MODEL slx_41d5be41e8e3
CONFIG AbsTol = auto
CONFIG EnableMultiTasking = off
CONFIG FixedStep = 1e-3
CONFIG MaxStep = auto
CONFIG MinStep = auto
CONFIG RelTol = 1e-3
CONFIG SampleTimeConstraint = Unconstrained
CONFIG Solver = ode14x
CONFIG SolverName = ode14x
CONFIG StartTime = 0.0
CONFIG StopTime = 15
BLOCK [From] Actual ouput
  GotoTag = Y
BLOCK [Scope] Actual position (mm)
  Floating = off
  NumInputPorts = 1
  Ports = [1]
  ScopeSpecificationString = Simulink.scopes.TimeScopeBlockCfg('CurrentConfiguration', extmgr.ConfigurationSet(extmgr.Configuration('Core','General UI',true),extmgr.Configuration('Core','Source UI',true),extmgr.Configuration('Sources','WiredSimulink',true,'DataLoggingVariableName','ScopeData1','DataLoggingSaveFormat','Array'),extmgr.Configuration('Visuals','Time Domain',true,'SerializedDisplays',{struct('MinYLimReal','-0.1145...<+1423ch>
BLOCK [Sum] Add
  IconShape = rectangular
  Inputs = +++
  Ports = [3, 1]
BLOCK [Derivative] Derivative
BLOCK [From] Disturbance Input
  GotoTag = D
BLOCK [From] Error
  GotoTag = E
BLOCK [Gain] Force to Voltage
  Gain = 1/ 2871.14
BLOCK [FromWorkspace] From Workspace2
  OutDataTypeStr = double
  OutputAfterFinalValue = Setting to zero
  VariableName = Cut1500down
BLOCK [Goto] Goto
  GotoTag = D
BLOCK [Goto] Goto1
  GotoTag = R
BLOCK [Goto] Goto2
  GotoTag = E
BLOCK [Goto] Goto3
  GotoTag = Y
BLOCK [Integrator] Integrator
  Ports = [1, 1]
BLOCK [Gain] Kd
  Gain = new_kd
BLOCK [Gain] Ki
  Gain = new_ki
BLOCK [Gain] Kp
  Gain = new_kp
BLOCK [ManualSwitch] Manual Switch2
  CurrentSetting = 0
  NameLocation = left
BLOCK [TransferFcn] Plant (Googol Tech)
  Denominator = [1 163 193.3]
  Numerator = [78020]
BLOCK [Sin] Ref. Position, Xref (mm)
  Amplitude = 5
  Frequency = 0.5*(2*pi)
  Offset = 1/2000
  Ports = [0, 1]
  SampleTime = 0
BLOCK [From] Reference Input
  GotoTag = R
BLOCK [Saturate] Saturation
  LowerLimit = -92
  UpperLimit = 92
BLOCK [Scope] Scope
  Floating = off
  NumInputPorts = 4
  Ports = [4]
  ScopeSpecificationString = Simulink.scopes.TimeScopeBlockCfg('CurrentConfiguration', extmgr.ConfigurationSet(extmgr.Configuration('Core','General UI',true),extmgr.Configuration('Core','Source UI',true),extmgr.Configuration('Sources','WiredSimulink',true,'DataLogging',true,'DataLoggingSaveFormat','StructureWithTime'),extmgr.Configuration('Visuals','Time Domain',true,'SerializedDisplays',{struct('MinYLimReal','-0.01731','MaxY...<+3810ch>
BLOCK [Sum] Sum
  Inputs = ++|
  Ports = [2, 1]
BLOCK [Sum] Sum1
  Inputs = |+-
  NameLocation = top
  Ports = [2, 1]
BLOCK [TransportDelay] TIme Delay
  DelayTime = 0.0012
  Ports = [1, 1]
LINE Actual ouput:1 -> Scope:4
LINE Add:1 -> Sum:2
LINE Derivative:1 -> Add:3
LINE Disturbance Input:1 -> Scope:1
LINE Error:1 -> Scope:2
LINE Force to Voltage:1 -> Goto:1
LINE Force to Voltage:1 -> Manual Switch2:1
LINE From Workspace2:1 -> Force to Voltage:1
LINE Integrator:1 -> Add:2
LINE Kd:1 -> Derivative:1
LINE Ki:1 -> Integrator:1
LINE Kp:1 -> Add:1
LINE Manual Switch2:1 -> Sum:1
LINE Plant (Googol Tech):1 -> TIme Delay:1
LINE Ref. Position, Xref (mm):1 -> Goto1:1
LINE Ref. Position, Xref (mm):1 -> Sum1:1
LINE Reference Input:1 -> Scope:3
LINE Saturation:1 -> Plant (Googol Tech):1
LINE Sum1:1 -> Goto2:1
LINE Sum1:1 -> Kd:1
LINE Sum1:1 -> Ki:1
LINE Sum1:1 -> Kp:1
LINE Sum:1 -> Saturation:1
LINE TIme Delay:1 -> Actual position (mm):1
LINE TIme Delay:1 -> Goto3:1
LINE TIme Delay:1 -> Sum1:2
